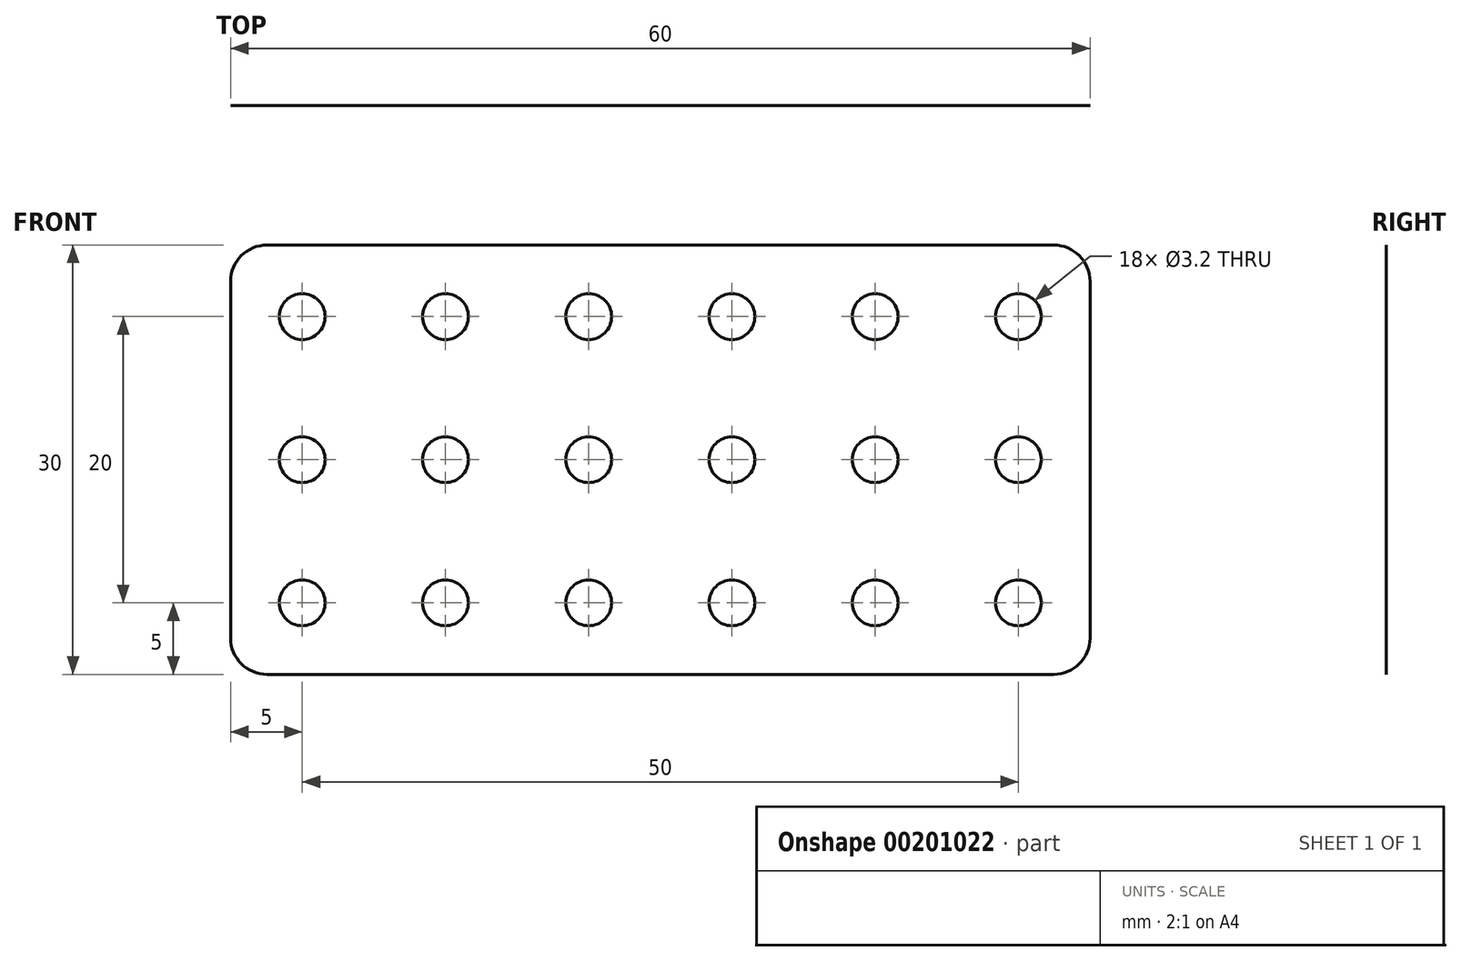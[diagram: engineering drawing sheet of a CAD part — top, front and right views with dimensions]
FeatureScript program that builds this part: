
annotation { "Feature Type Name" : "Feature", "Feature Type Description" : "" }
export const myFeature = defineFeature(function(context is Context, id is Id, definition is map)
    precondition{}
    {
        {
            var Q0;
            Q0=qCreatedBy(makeId("Front.planeOp"),FACE);
            var sketch = newSketch(context, id + "F0", { "sketchPlane" : qUnion([Q0])});
            skLineSegment(sketch, "E0.bottom", {"start": v(2.54, 0) * mm, "end": v(57.46, 0) * mm});
            skLineSegment(sketch, "E0.top", {"start": v(2.54, -30) * mm, "end": v(57.46, -30) * mm});
            skLineSegment(sketch, "E0.left", {"start": v(0, -2.54) * mm, "end": v(0, -27.46) * mm});
            skLineSegment(sketch, "E0.right", {"start": v(60, -2.54) * mm, "end": v(60, -27.46) * mm});
            skCircle(sketch, "E1", {"center": v(5, -5) * mm, "radius": 1.6 * mm});
            skPoint(sketch, "E2.visualSharp", {"position": v(0, 0) * mm});
            skArc(sketch, "E2.filletArc", {"start": v(2.54, 0) * mm, "mid": v(0.74, -0.74) * mm, "end": v(0, -2.54) * mm});
            skPoint(sketch, "E3.visualSharp", {"position": v(60, 0) * mm});
            skArc(sketch, "E3.filletArc", {"start": v(60, -2.54) * mm, "mid": v(59.26, -0.74) * mm, "end": v(57.46, 0) * mm});
            skPoint(sketch, "E4.visualSharp", {"position": v(60, -30) * mm});
            skArc(sketch, "E4.filletArc", {"start": v(57.46, -30) * mm, "mid": v(59.26, -29.26) * mm, "end": v(60, -27.46) * mm});
            skPoint(sketch, "E5.visualSharp", {"position": v(0, -30) * mm});
            skArc(sketch, "E5.filletArc", {"start": v(0, -27.46) * mm, "mid": v(0.74, -29.26) * mm, "end": v(2.54, -30) * mm});
            skCircle(sketch, "E6.0.1.0", {"center": v(5, -15) * mm, "radius": 1.6 * mm});
            skCircle(sketch, "E6.0.2.0", {"center": v(5, -25) * mm, "radius": 1.6 * mm});
            skCircle(sketch, "E6.1.0.0", {"center": v(15, -5) * mm, "radius": 1.6 * mm});
            skCircle(sketch, "E6.1.1.0", {"center": v(15, -15) * mm, "radius": 1.6 * mm});
            skCircle(sketch, "E6.1.2.0", {"center": v(15, -25) * mm, "radius": 1.6 * mm});
            skCircle(sketch, "E6.2.0.0", {"center": v(25, -5) * mm, "radius": 1.6 * mm});
            skCircle(sketch, "E6.2.1.0", {"center": v(25, -15) * mm, "radius": 1.6 * mm});
            skCircle(sketch, "E6.2.2.0", {"center": v(25, -25) * mm, "radius": 1.6 * mm});
            skCircle(sketch, "E6.3.0.0", {"center": v(35, -5) * mm, "radius": 1.6 * mm});
            skCircle(sketch, "E6.3.1.0", {"center": v(35, -15) * mm, "radius": 1.6 * mm});
            skCircle(sketch, "E6.3.2.0", {"center": v(35, -25) * mm, "radius": 1.6 * mm});
            skCircle(sketch, "E6.4.0.0", {"center": v(45, -5) * mm, "radius": 1.6 * mm});
            skCircle(sketch, "E6.4.1.0", {"center": v(45, -15) * mm, "radius": 1.6 * mm});
            skCircle(sketch, "E6.4.2.0", {"center": v(45, -25) * mm, "radius": 1.6 * mm});
            skCircle(sketch, "E6.5.0.0", {"center": v(55, -5) * mm, "radius": 1.6 * mm});
            skCircle(sketch, "E6.5.1.0", {"center": v(55, -15) * mm, "radius": 1.6 * mm});
            skCircle(sketch, "E6.5.2.0", {"center": v(55, -25) * mm, "radius": 1.6 * mm});
            skLineSegment(sketch, "E6.direction1", {"start": v(5, -5) * mm, "end": v(15, -5) * mm, "construction": true});
            skLineSegment(sketch, "E6.direction2", {"start": v(5, -5) * mm, "end": v(5, -15) * mm, "construction": true});
            skSolve(sketch);
        }
        {
            var Q0;
            Q0=makeQuery(id+"F0.imprint","IMPRINT",FACE,{"disambiguationData":[TD([[makeQuery(id+"F0.imprint","IMPRINT",EDGE,{"derivedFrom":sQuery(id+"F0.wireOp",EDGE,"E0.bottom")}),-1.0]])]});
            extrude(context, id + "F1", {"entities" : qUnion([Q0]), "depth" : 1 / 203.2 * mm});
        }
    });
